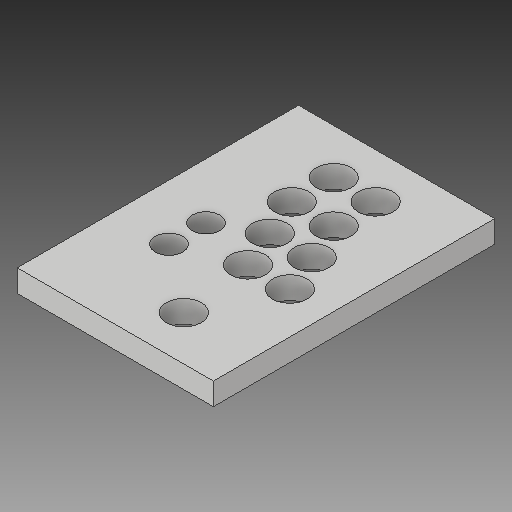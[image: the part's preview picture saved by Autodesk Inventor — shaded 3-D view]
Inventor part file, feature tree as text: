
AUTODESK INVENTOR PART (.ipt)
format: ipt  version: 2017 (Build 210142000, 142)  size: 159,232 bytes
history: native  units: in
note: dims shown in document units (in); Inventor stores cm internally (conversion verified against a paired STEP export)
features: extrude x2, sketch x2
ambient origin geometry x8: Origin, YZ Plane, XZ Plane, XY Plane, X Axis, Y Axis, Z Axis, Center Point
bodies: Solid1 (feature_tree)
feature tree (4):
  extrude  "Extrusion1"  Depth=9.5in
  extrude  "Extrusion2"  Depth=0.75in
  sketch  "Sketch1"  dims[d0=6.625in d1=9.5in]
  sketch  "Sketch2"  dims[d2=0.75in d3=0.0in d4=1.18in d5=1.18in d6=1.18in d7=1.18in d8=1.18in d9=1.18in d10=1.18in d11=1.18in d12=1.18in d13=2.48in d14=2.48in d15=1.29in d16=1.29in d17=1.29in d18=1.29in d19=1.417in d20=1.417in d22=0.55in d23=0.55in d24=0.315in d25=0.315in d26=0.55in d27=0.55in d28=0.55in d29=1.5in d30=0.925in d31=3.25in d33=0.925in d35=1.25in d36=1.0in d37=0.0in d38=2.5in d39=0.315in d40=4.75in d41=4.75in]
